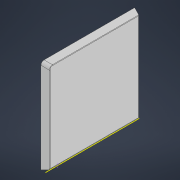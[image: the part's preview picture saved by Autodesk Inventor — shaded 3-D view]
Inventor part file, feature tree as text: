
AUTODESK INVENTOR PART (.ipt)
format: ipt  version: 2022 (Build 260153070, 153G)  size: 120,320 bytes
history: native  units: mm
features: other x5, sketch x3, chamfer x2, fillet x2, extrude x1
ambient origin geometry x8: Origin, YZ Plane, XZ Plane, XY Plane, X Axis, Y Axis, Z Axis, Center Point
bodies: Body1 (feature_tree)
feature tree (13):
  other  "Твердое тело1"
  other  "РабПлоскость1"
  extrude  "Выдавливание1"  Depth=16.0mm TaperAngle=0.0deg
  chamfer  "Фаска1"  Distance=16.0mm Angle=45.0deg
  sketch  "Эскиз2"
  sketch  "Эскиз3"
  chamfer  "Фаска2"  Distance=341.0mm
  fillet  "Сопряжение1"  Radius=341.0mm
  fillet  "Сопряжение2"  Radius=16.0mm
  sketch  "Эскиз1"
  other  "<userpath>\Documents\Inventor\TUTO\N_core.iam"
  other  "N_core.iam"
  other  "N_into_side:1"
